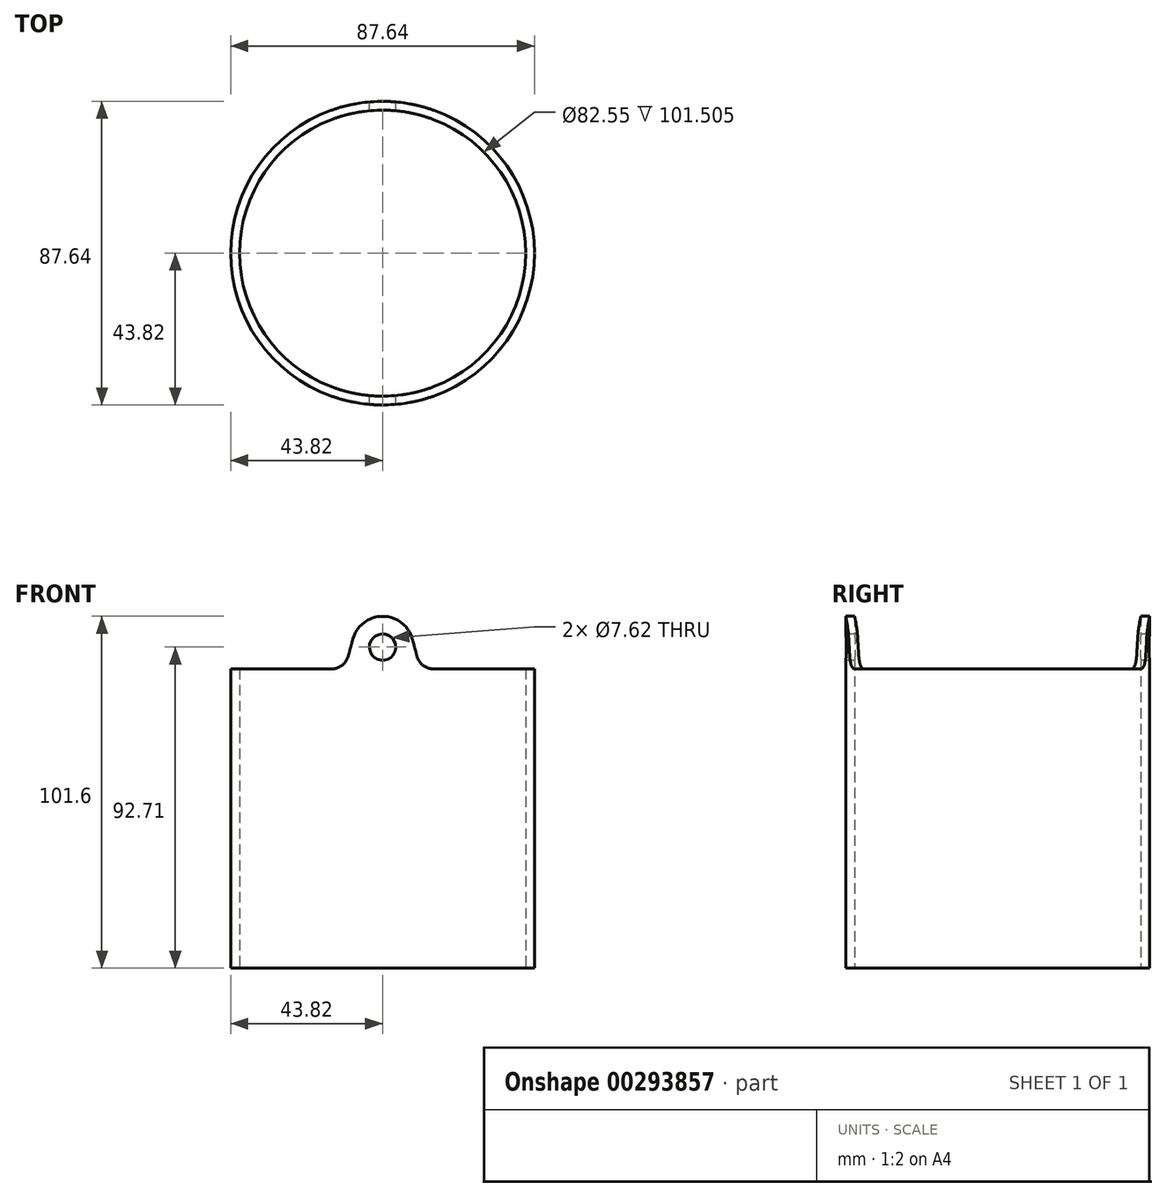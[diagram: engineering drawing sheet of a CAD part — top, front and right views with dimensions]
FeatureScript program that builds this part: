
annotation { "Feature Type Name" : "Feature", "Feature Type Description" : "" }
export const myFeature = defineFeature(function(context is Context, id is Id, definition is map)
    precondition{}
    {
        {
            assignVariable(context, id + "F0", {"name" : "thk", "anyValue" : .10});
        }
        {
            var Q0;
            Q0=qCreatedBy(makeId("Top.planeOp"),FACE);
            var sketch = newSketch(context, id + "F1", { "sketchPlane" : qUnion([Q0])});
            skCircle(sketch, "E0", {"center": v(0, 0) * mm, "radius": 41.28 * mm});
            skCircle(sketch, "E1.converted", {"center": v(0, 0) * mm, "radius": 43.82 * mm});
            skSolve(sketch);
        }
        {
            var Q0;
            Q0=makeQuery(id+"F1.imprint","IMPRINT",FACE,{"disambiguationData":[TD([[makeQuery(id+"F1.imprint","IMPRINT",EDGE,{"derivedFrom":sQuery(id+"F1.wireOp",EDGE,"E0")}),-1.0]])]});
            extrude(context, id + "F2", {"entities" : qUnion([Q0]), "depth" : 101.6 * mm});
        }
        {
            var Q0;
            Q0=makeQuery(id+"F1.imprint","IMPRINT",FACE,{"disambiguationData":[TD([[makeQuery(id+"F1.imprint","IMPRINT",EDGE,{"derivedFrom":sQuery(id+"F1.wireOp",EDGE,"E0")}),1.0]])]});
            extrude(context, id + "F3", {"entities" : qUnion([Q0]), "operationType" : NewBodyOperationType.ADD, "depth" : (getVariable(context, 'thk')) * mm});
        }
        {
            var Q0;
            Q0=qCreatedBy(makeId("Front.planeOp"),FACE);
            var sketch = newSketch(context, id + "F4", { "sketchPlane" : qUnion([Q0])});
            skCircle(sketch, "E2", {"center": v(0, 92.7) * mm, "radius": 3.81 * mm});
            skLineSegment(sketch, "E3", {"start": v(-46.66, 104.18) * mm, "end": v(-46.66, 86.36) * mm});
            skLineSegment(sketch, "E4", {"start": v(-46.66, 86.36) * mm, "end": v(-10.9, 86.36) * mm});
            skLineSegment(sketch, "E5", {"start": v(-10.9, 86.36) * mm, "end": v(-8.59, 95.01) * mm});
            skLineSegment(sketch, "E6", {"start": v(8.59, 95.01) * mm, "end": v(10.9, 86.36) * mm});
            skLineSegment(sketch, "E7", {"start": v(10.9, 86.36) * mm, "end": v(46.66, 86.36) * mm});
            skLineSegment(sketch, "E8", {"start": v(46.66, 86.36) * mm, "end": v(46.66, 104.18) * mm});
            skLineSegment(sketch, "E9", {"start": v(46.66, 104.18) * mm, "end": v(-46.66, 104.18) * mm});
            skArc(sketch, "E10", {"start": v(8.59, 95.01) * mm, "mid": v(0, 101.6) * mm, "end": v(-8.59, 95.01) * mm});
            skSolve(sketch);
        }
        {
            var Q0;
            Q0=makeQuery(id+"F4.imprint","IMPRINT",FACE,{"disambiguationData":[TD([[makeQuery(id+"F4.imprint","IMPRINT",EDGE,{"derivedFrom":sQuery(id+"F4.wireOp",EDGE,"E2")}),1.0]])]});
            var Q1;
            Q1=makeQuery(id+"F4.imprint","IMPRINT",FACE,{"disambiguationData":[TD([[makeQuery(id+"F4.imprint","IMPRINT",EDGE,{"derivedFrom":sQuery(id+"F4.wireOp",EDGE,"E3")}),1.0]])]});
            extrude(context, id + "F5", {"entities" : qUnion([Q0, Q1]), "operationType" : NewBodyOperationType.REMOVE, "endBound" : BoundingType.SYMMETRIC, "depth" : 115.32 * mm});
        }
        {
            var Q0;
            Q0=makeQuery(id+"F5.boolean.opBoolean","COPY",EDGE,{"disambiguationData":[OD(0.0)],"derivedFrom":makeQuery(id+"F5.opExtrude","SWEPT_EDGE",EDGE,{"disambiguationData":[OSD([sQuery(id+"F4.wireOp",EDGE,"E6"),sQuery(id+"F4.wireOp",EDGE,"E7")])]})});
            var Q1;
            Q1=makeQuery(id+"F5.boolean.opBoolean","COPY",EDGE,{"disambiguationData":[OD(0.0)],"derivedFrom":makeQuery(id+"F5.opExtrude","SWEPT_EDGE",EDGE,{"disambiguationData":[OSD([sQuery(id+"F4.wireOp",EDGE,"E4"),sQuery(id+"F4.wireOp",EDGE,"E5")])]})});
            var Q2;
            Q2=makeQuery(id+"F5.boolean.opBoolean","COPY",EDGE,{"disambiguationData":[OD(1.0)],"derivedFrom":makeQuery(id+"F5.opExtrude","SWEPT_EDGE",EDGE,{"disambiguationData":[OSD([sQuery(id+"F4.wireOp",EDGE,"E6"),sQuery(id+"F4.wireOp",EDGE,"E7")])]})});
            var Q3;
            Q3=makeQuery(id+"F5.boolean.opBoolean","COPY",EDGE,{"disambiguationData":[OD(1.0)],"derivedFrom":makeQuery(id+"F5.opExtrude","SWEPT_EDGE",EDGE,{"disambiguationData":[OSD([sQuery(id+"F4.wireOp",EDGE,"E4"),sQuery(id+"F4.wireOp",EDGE,"E5")])]})});
            fillet(context, id + "F6", {"entities" : qUnion([Q0, Q1, Q2, Q3]), "radius" : 5.08 * mm, "tangentPropagation" : true, "allowEdgeOverflow" : false});
        }
    });
